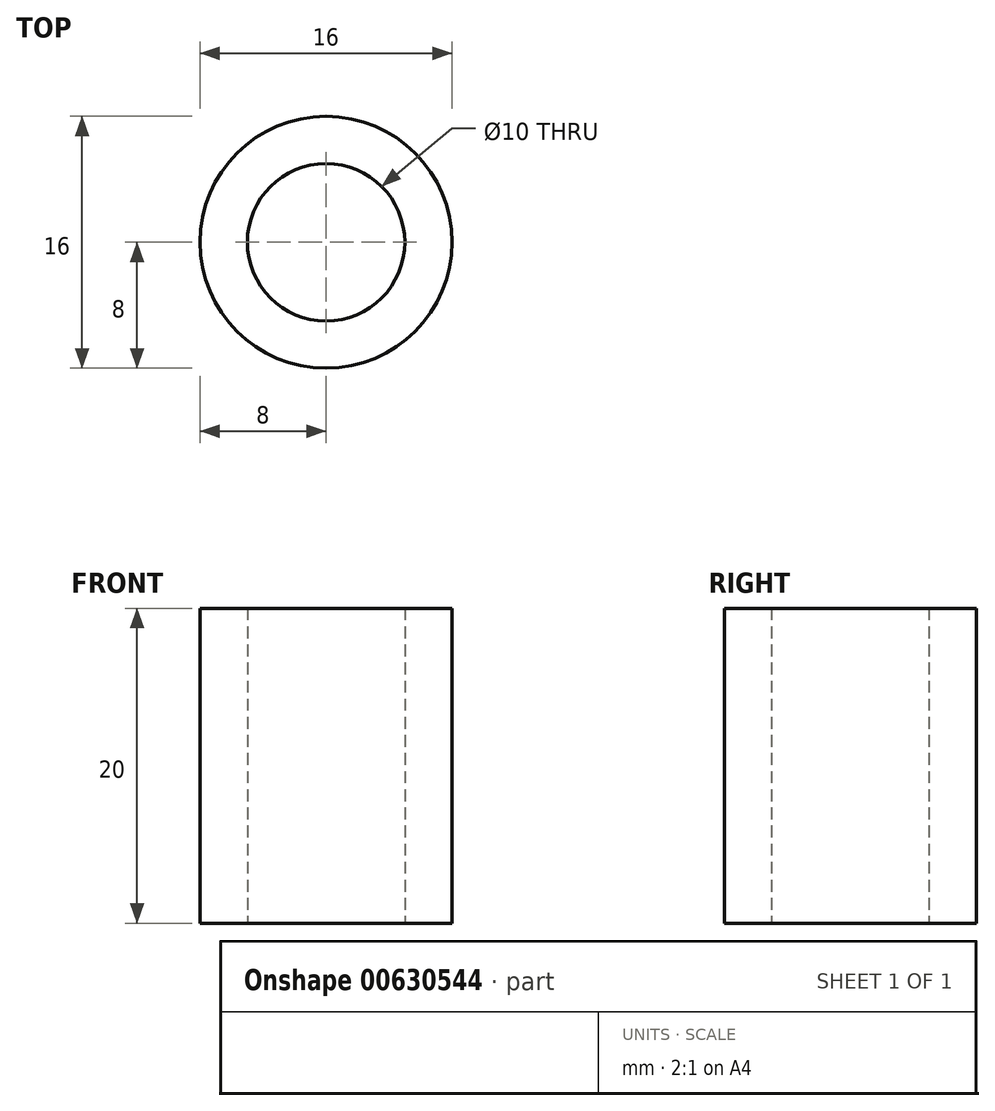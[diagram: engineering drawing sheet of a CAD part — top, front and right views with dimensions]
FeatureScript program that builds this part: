
annotation { "Feature Type Name" : "Feature", "Feature Type Description" : "" }
export const myFeature = defineFeature(function(context is Context, id is Id, definition is map)
    precondition{}
    {
        {
            var Q0;
            Q0=qCreatedBy(makeId("Top.planeOp"),FACE);
            var sketch = newSketch(context, id + "F0", { "sketchPlane" : qUnion([Q0])});
            skCircle(sketch, "E0", {"center": v(0, 0) * mm, "radius": 5 * mm});
            skCircle(sketch, "E1", {"center": v(0, 0) * mm, "radius": 8 * mm});
            skSolve(sketch);
        }
        {
            var Q0;
            Q0=makeQuery(id+"F0.imprint","IMPRINT",FACE,{"disambiguationData":[TD([[makeQuery(id+"F0.imprint","IMPRINT",EDGE,{"derivedFrom":sQuery(id+"F0.wireOp",EDGE,"E0")}),-1.0]])]});
            extrude(context, id + "F1", {"entities" : qUnion([Q0]), "depth" : 20 * mm, "offsetDistance" : 25 * mm});
        }
    });
